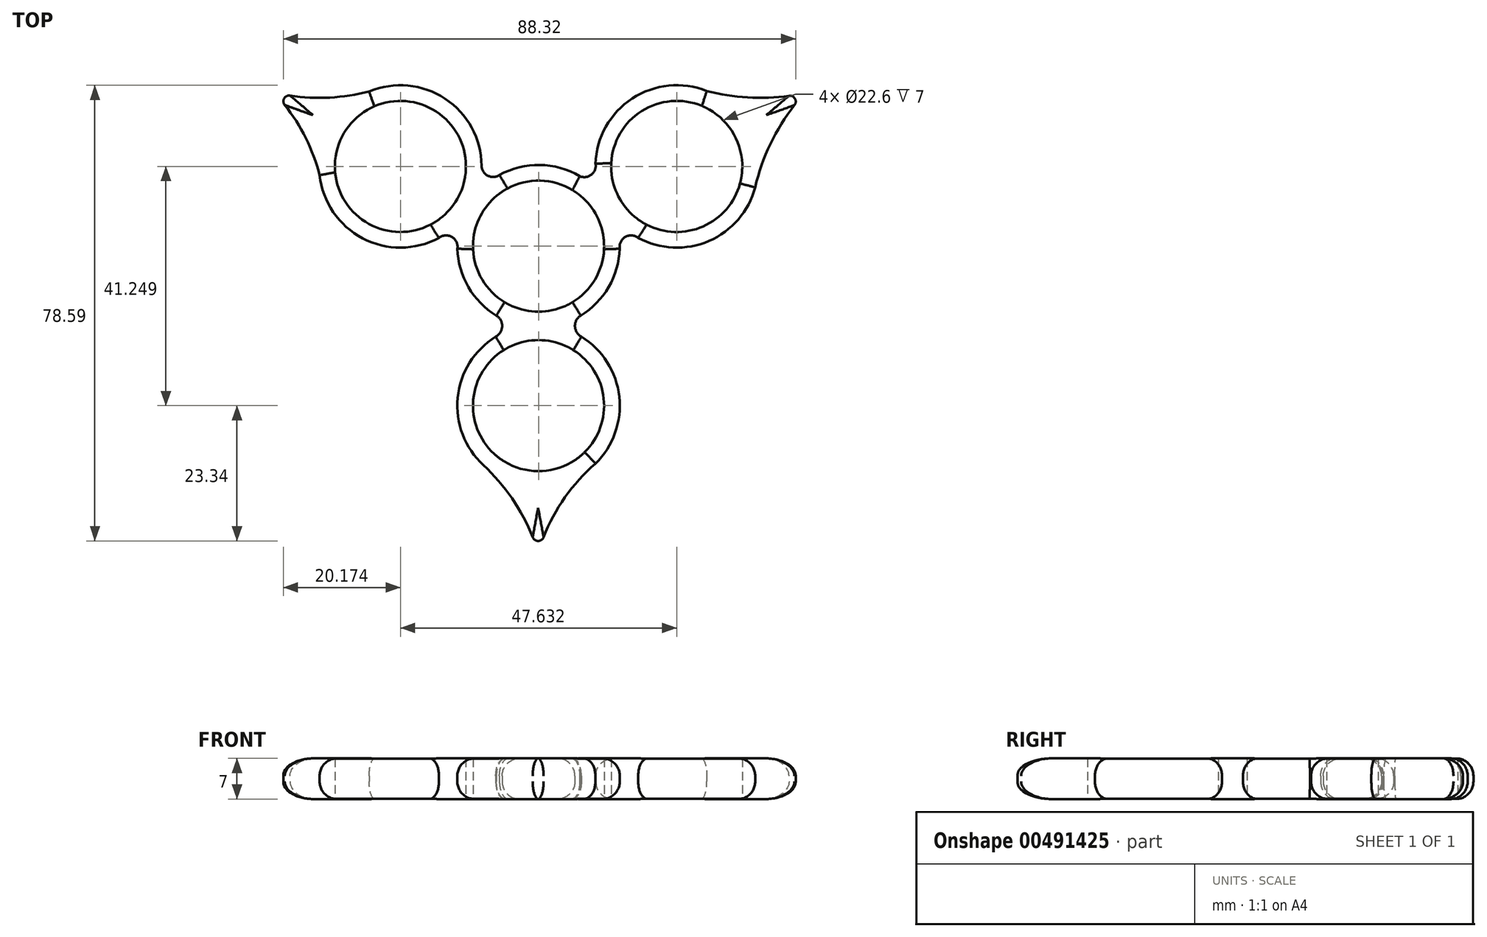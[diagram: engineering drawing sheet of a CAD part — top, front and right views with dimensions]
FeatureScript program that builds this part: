
annotation { "Feature Type Name" : "Feature", "Feature Type Description" : "" }
export const myFeature = defineFeature(function(context is Context, id is Id, definition is map)
    precondition{}
    {
        {
            var Q0;
            Q0=qCreatedBy(makeId("Top.planeOp"),FACE);
            var sketch = newSketch(context, id + "F0", { "sketchPlane" : qUnion([Q0])});
            skCircle(sketch, "E0", {"center": v(0, 0) * mm, "radius": 11.3 * mm});
            skCircle(sketch, "E1", {"center": v(0, 0) * mm, "radius": 14 * mm});
            skCircle(sketch, "E2", {"center": v(0, 0) * mm, "radius": 27.5 * mm});
            skCircle(sketch, "E3", {"center": v(-23.82, 13.75) * mm, "radius": 11.3 * mm});
            skCircle(sketch, "E4", {"center": v(23.82, 13.75) * mm, "radius": 11.3 * mm});
            skCircle(sketch, "E5", {"center": v(0, -27.5) * mm, "radius": 11.3 * mm});
            skCircle(sketch, "E6", {"center": v(-23.82, 13.75) * mm, "radius": 14 * mm});
            skCircle(sketch, "E7", {"center": v(23.82, 13.75) * mm, "radius": 14 * mm});
            skCircle(sketch, "E8", {"center": v(0, -27.5) * mm, "radius": 14 * mm});
            skArc(sketch, "E9", {"start": v(7.27, -11.97) * mm, "mid": v(6.28, -13.82) * mm, "end": v(7.38, -15.6) * mm});
            skArc(sketch, "E10", {"start": v(-7.38, -15.6) * mm, "mid": v(-6.28, -13.82) * mm, "end": v(-7.27, -11.97) * mm});
            skArc(sketch, "E11", {"start": v(6.74, 12.27) * mm, "mid": v(8.93, 12.2) * mm, "end": v(9.82, 14.2) * mm});
            skArc(sketch, "E12", {"start": v(-9.82, 13.87) * mm, "mid": v(-8.76, 12.15) * mm, "end": v(-6.74, 12.27) * mm});
            skArc(sketch, "E13", {"start": v(-14, -0.42) * mm, "mid": v(-14.95, 1.6) * mm, "end": v(-17.18, 1.42) * mm});
            skPoint(sketch, "E13.endSnap0", {"position": v(14.99, 1.42) * mm});
            skArc(sketch, "E14", {"start": v(17.18, 1.42) * mm, "mid": v(14.95, 1.6) * mm, "end": v(14, -0.42) * mm});
            skArc(sketch, "E15", {"start": v(-0.06, -52.92) * mm, "mid": v(-3.88, -44.54) * mm, "end": v(-9.82, -37.5) * mm});
            skArc(sketch, "E16", {"start": v(9.8, -37.5) * mm, "mid": v(3.76, -44.5) * mm, "end": v(-0.06, -52.92) * mm});
            skLineSegment(sketch, "E17", {"start": v(0, 0) * mm, "end": v(45.87, 26.4) * mm});
            skLineSegment(sketch, "E18", {"start": v(0, 0) * mm, "end": v(-0.06, -52.92) * mm});
            skLineSegment(sketch, "E19", {"start": v(0, 0) * mm, "end": v(-45.77, 26.56) * mm});
            skArc(sketch, "E20", {"start": v(-45.66, 26.52) * mm, "mid": v(-36.5, 25.6) * mm, "end": v(-27.41, 27.19) * mm});
            skArc(sketch, "E21", {"start": v(-37.28, 10.23) * mm, "mid": v(-40.3, 18.98) * mm, "end": v(-45.66, 26.52) * mm});
            skLineSegment(sketch, "E22", {"start": v(27.55, 27.16) * mm, "end": v(37.35, 10.15) * mm});
            skArc(sketch, "E23", {"start": v(45.87, 26.4) * mm, "mid": v(40.57, 18.82) * mm, "end": v(37.35, 10.15) * mm});
            skArc(sketch, "E24", {"start": v(27.55, 27.16) * mm, "mid": v(36.66, 25.62) * mm, "end": v(45.87, 26.4) * mm});
            skSolve(sketch);
        }
        {
            var Q0;
            {var subQ0=sQuery(id+"F0.wireOp",EDGE,"E7");var subQ1=sQuery(id+"F0.wireOp",EDGE,"E2");var subQ2=makeQuery(id+"F0.imprint","INTERSECT",VERTEX,{"disambiguationData":[OD(0.0)],"derivedFrom":[subQ1,subQ0]});Q0=makeQuery(id+"F0.imprint","IMPRINT",FACE,{"disambiguationData":[TD([[makeQuery(id+"F0.imprint","IMPRINT",EDGE,{"disambiguationData":[TD([[subQ2,-1.0]])],"derivedFrom":subQ1}),-1.0]])]});}
            var Q1;
            {var subQ0=sQuery(id+"F0.wireOp",EDGE,"E6");var subQ1=sQuery(id+"F0.wireOp",EDGE,"E2");var subQ2=makeQuery(id+"F0.imprint","INTERSECT",VERTEX,{"disambiguationData":[OD(0.0)],"derivedFrom":[subQ1,subQ0]});Q1=makeQuery(id+"F0.imprint","IMPRINT",FACE,{"disambiguationData":[TD([[makeQuery(id+"F0.imprint","IMPRINT",EDGE,{"disambiguationData":[TD([[subQ2,-1.0]])],"derivedFrom":subQ1}),-1.0]])]});}
            var Q2;
            {var subQ0=sQuery(id+"F0.wireOp",EDGE,"E8");var subQ1=sQuery(id+"F0.wireOp",EDGE,"E2");var subQ2=makeQuery(id+"F0.imprint","INTERSECT",VERTEX,{"disambiguationData":[OD(0.0)],"derivedFrom":[subQ1,subQ0]});Q2=makeQuery(id+"F0.imprint","IMPRINT",FACE,{"disambiguationData":[TD([[makeQuery(id+"F0.imprint","IMPRINT",EDGE,{"disambiguationData":[TD([[subQ2,-1.0]])],"derivedFrom":subQ1}),-1.0]])]});}
            var Q3;
            {var subQ0=sQuery(id+"F0.wireOp",EDGE,"E7");var subQ1=sQuery(id+"F0.wireOp",EDGE,"E1");var subQ2=makeQuery(id+"F0.imprint","INTERSECT",VERTEX,{"disambiguationData":[OD(0.0)],"derivedFrom":[subQ1,subQ0]});Q3=makeQuery(id+"F0.imprint","IMPRINT",FACE,{"disambiguationData":[TD([[makeQuery(id+"F0.imprint","IMPRINT",EDGE,{"disambiguationData":[TD([[subQ2,1.0]])],"derivedFrom":subQ1}),-1.0]])]});}
            var Q4;
            {var subQ4=sQuery(id+"F0.wireOp",EDGE,"E8");var subQ10=sQuery(id+"F0.wireOp",EDGE,"E1");var subQ11=makeQuery(id+"F0.imprint","INTERSECT",VERTEX,{"disambiguationData":[OD(0.0)],"derivedFrom":[subQ10,subQ4]});Q4=makeQuery(id+"F0.imprint","IMPRINT",FACE,{"disambiguationData":[TD([[makeQuery(id+"F0.imprint","IMPRINT",EDGE,{"disambiguationData":[TD([[subQ11,-1.0]])],"derivedFrom":subQ10}),-1.0]])]});}
            var Q5;
            {var subQ0=sQuery(id+"F0.wireOp",EDGE,"E11");var subQ1=sQuery(id+"F0.wireOp",EDGE,"E1");var subQ2=makeQuery(id+"F0.imprint","INTERSECT",VERTEX,{"derivedFrom":[subQ1,subQ0]});Q5=makeQuery(id+"F0.imprint","IMPRINT",FACE,{"disambiguationData":[TD([[makeQuery(id+"F0.imprint","IMPRINT",EDGE,{"disambiguationData":[TD([[subQ2,1.0]])],"derivedFrom":subQ1}),-1.0]])]});}
            var Q6;
            {var subQ0=sQuery(id+"F0.wireOp",EDGE,"E6");var subQ1=sQuery(id+"F0.wireOp",EDGE,"E1");var subQ2=makeQuery(id+"F0.imprint","INTERSECT",VERTEX,{"disambiguationData":[OD(0.0)],"derivedFrom":[subQ1,subQ0]});Q6=makeQuery(id+"F0.imprint","IMPRINT",FACE,{"disambiguationData":[TD([[makeQuery(id+"F0.imprint","IMPRINT",EDGE,{"disambiguationData":[TD([[subQ2,-1.0]])],"derivedFrom":subQ1}),1.0]])]});}
            var Q7;
            {var subQ0=sQuery(id+"F0.wireOp",EDGE,"E9");var subQ1=sQuery(id+"F0.wireOp",EDGE,"E1");var subQ2=makeQuery(id+"F0.imprint","INTERSECT",VERTEX,{"derivedFrom":[subQ1,subQ0]});Q7=makeQuery(id+"F0.imprint","IMPRINT",FACE,{"disambiguationData":[TD([[makeQuery(id+"F0.imprint","IMPRINT",EDGE,{"disambiguationData":[TD([[subQ2,1.0]])],"derivedFrom":subQ1}),-1.0]])]});}
            var Q8;
            {var subQ0=sQuery(id+"F0.wireOp",EDGE,"E10");var subQ1=sQuery(id+"F0.wireOp",EDGE,"E1");var subQ2=makeQuery(id+"F0.imprint","INTERSECT",VERTEX,{"derivedFrom":[subQ1,subQ0]});Q8=makeQuery(id+"F0.imprint","IMPRINT",FACE,{"disambiguationData":[TD([[makeQuery(id+"F0.imprint","IMPRINT",EDGE,{"disambiguationData":[TD([[subQ2,-1.0]])],"derivedFrom":subQ1}),-1.0]])]});}
            var Q9;
            {var subQ0=sQuery(id+"F0.wireOp",EDGE,"E7");var subQ10=sQuery(id+"F0.wireOp",EDGE,"E1");var subQ11=makeQuery(id+"F0.imprint","INTERSECT",VERTEX,{"disambiguationData":[OD(0.0)],"derivedFrom":[subQ10,subQ0]});Q9=makeQuery(id+"F0.imprint","IMPRINT",FACE,{"disambiguationData":[TD([[makeQuery(id+"F0.imprint","IMPRINT",EDGE,{"disambiguationData":[TD([[subQ11,-1.0]])],"derivedFrom":subQ10}),-1.0]])]});}
            var Q10;
            Q10=makeQuery(id+"F0.imprint","IMPRINT",FACE,{"disambiguationData":[TD([[makeQuery(id+"F0.imprint","IMPRINT",EDGE,{"derivedFrom":sQuery(id+"F0.wireOp",EDGE,"E0")}),-1.0]])]});
            var Q11;
            Q11=makeQuery(id+"F0.imprint","IMPRINT",FACE,{"disambiguationData":[TD([[makeQuery(id+"F0.imprint","IMPRINT",EDGE,{"derivedFrom":sQuery(id+"F0.wireOp",EDGE,"E0")}),-1.0]])]});
            var Q12;
            {var subQ0=sQuery(id+"F0.wireOp",EDGE,"E8");var subQ1=sQuery(id+"F0.wireOp",EDGE,"E1");var subQ2=makeQuery(id+"F0.imprint","INTERSECT",VERTEX,{"disambiguationData":[OD(0.0)],"derivedFrom":[subQ1,subQ0]});Q12=makeQuery(id+"F0.imprint","IMPRINT",FACE,{"disambiguationData":[TD([[makeQuery(id+"F0.imprint","IMPRINT",EDGE,{"disambiguationData":[TD([[subQ2,-1.0]])],"derivedFrom":subQ1}),1.0]])]});}
            var Q13;
            {var subQ4=sQuery(id+"F0.wireOp",EDGE,"E6");var subQ9=sQuery(id+"F0.wireOp",EDGE,"E1");var subQ10=makeQuery(id+"F0.imprint","INTERSECT",VERTEX,{"disambiguationData":[OD(0.0)],"derivedFrom":[subQ9,subQ4]});Q13=makeQuery(id+"F0.imprint","IMPRINT",FACE,{"disambiguationData":[TD([[makeQuery(id+"F0.imprint","IMPRINT",EDGE,{"disambiguationData":[TD([[subQ10,-1.0]])],"derivedFrom":subQ9}),-1.0]])]});}
            var Q14;
            {var subQ0=sQuery(id+"F0.wireOp",EDGE,"E12");var subQ1=sQuery(id+"F0.wireOp",EDGE,"E1");var subQ2=makeQuery(id+"F0.imprint","INTERSECT",VERTEX,{"disambiguationData":[OD(1.0)],"derivedFrom":[subQ1,subQ0]});Q14=makeQuery(id+"F0.imprint","IMPRINT",FACE,{"disambiguationData":[TD([[makeQuery(id+"F0.imprint","IMPRINT",EDGE,{"disambiguationData":[TD([[subQ2,-1.0]])],"derivedFrom":subQ1}),-1.0]])]});}
            var Q15;
            {var subQ0=sQuery(id+"F0.wireOp",EDGE,"E6");var subQ1=sQuery(id+"F0.wireOp",EDGE,"E1");var subQ2=makeQuery(id+"F0.imprint","INTERSECT",VERTEX,{"disambiguationData":[OD(1.0)],"derivedFrom":[subQ1,subQ0]});Q15=makeQuery(id+"F0.imprint","IMPRINT",FACE,{"disambiguationData":[TD([[makeQuery(id+"F0.imprint","IMPRINT",EDGE,{"disambiguationData":[TD([[subQ2,-1.0]])],"derivedFrom":subQ1}),-1.0]])]});}
            var Q16;
            {var subQ0=sQuery(id+"F0.wireOp",EDGE,"E7");var subQ1=sQuery(id+"F0.wireOp",EDGE,"E1");var subQ2=makeQuery(id+"F0.imprint","INTERSECT",VERTEX,{"disambiguationData":[OD(0.0)],"derivedFrom":[subQ1,subQ0]});Q16=makeQuery(id+"F0.imprint","IMPRINT",FACE,{"disambiguationData":[TD([[makeQuery(id+"F0.imprint","IMPRINT",EDGE,{"disambiguationData":[TD([[subQ2,-1.0]])],"derivedFrom":subQ1}),1.0]])]});}
            var Q17;
            {var subQ0=sQuery(id+"F0.wireOp",EDGE,"E7");var subQ1=sQuery(id+"F0.wireOp",EDGE,"E2");var subQ2=makeQuery(id+"F0.imprint","INTERSECT",VERTEX,{"disambiguationData":[OD(1.0)],"derivedFrom":[subQ1,subQ0]});Q17=makeQuery(id+"F0.imprint","IMPRINT",FACE,{"disambiguationData":[TD([[makeQuery(id+"F0.imprint","IMPRINT",EDGE,{"disambiguationData":[TD([[subQ2,1.0]])],"derivedFrom":subQ1}),-1.0]])]});}
            var Q18;
            {var subQ1=sQuery(id+"F0.wireOp",EDGE,"3PTmMetB-9Mq9-OfqD-WaSR-vOR6SDGipExO.left");var subQ4=sQuery(id+"F0.wireOp",EDGE,"E4");var subQ5=makeQuery(id+"F0.imprint","INTERSECT",VERTEX,{"derivedFrom":[subQ4,subQ1]});Q18=makeQuery(id+"F0.imprint","IMPRINT",FACE,{"disambiguationData":[TD([[makeQuery(id+"F0.imprint","IMPRINT",EDGE,{"disambiguationData":[TD([[subQ5,1.0]])],"derivedFrom":subQ4}),-1.0]])]});}
            var Q19;
            {var subQ1=sQuery(id+"F0.wireOp",EDGE,"9Et0mAI1-HBt8-Chc9-DNCY-ShBSqTFfpHgo.left");var subQ4=sQuery(id+"F0.wireOp",EDGE,"E3");var subQ5=makeQuery(id+"F0.imprint","INTERSECT",VERTEX,{"derivedFrom":[subQ4,subQ1]});Q19=makeQuery(id+"F0.imprint","IMPRINT",FACE,{"disambiguationData":[TD([[makeQuery(id+"F0.imprint","IMPRINT",EDGE,{"disambiguationData":[TD([[subQ5,-1.0]])],"derivedFrom":subQ4}),-1.0]])]});}
            var Q20;
            {var subQ0=sQuery(id+"F0.wireOp",EDGE,"E6");var subQ1=sQuery(id+"F0.wireOp",EDGE,"E2");var subQ2=makeQuery(id+"F0.imprint","INTERSECT",VERTEX,{"disambiguationData":[OD(1.0)],"derivedFrom":[subQ1,subQ0]});Q20=makeQuery(id+"F0.imprint","IMPRINT",FACE,{"disambiguationData":[TD([[makeQuery(id+"F0.imprint","IMPRINT",EDGE,{"disambiguationData":[TD([[subQ2,1.0]])],"derivedFrom":subQ1}),-1.0]])]});}
            var Q21;
            {var subQ0=sQuery(id+"F0.wireOp",EDGE,"0O0kyQyX-SNUq-BMQf-ScT6-pGwFIUG6Fi4E");var subQ1=sQuery(id+"F0.wireOp",EDGE,"E6");var subQ2=makeQuery(id+"F0.imprint","INTERSECT",VERTEX,{"derivedFrom":[subQ1,subQ0]});Q21=makeQuery(id+"F0.imprint","IMPRINT",FACE,{"disambiguationData":[TD([[makeQuery(id+"F0.imprint","IMPRINT",EDGE,{"disambiguationData":[TD([[subQ2,-1.0]])],"derivedFrom":subQ1}),-1.0]])]});}
            var Q22;
            {var subQ0=sQuery(id+"F0.wireOp",EDGE,"E15");var subQ1=sQuery(id+"F0.wireOp",EDGE,"E8");var subQ2=makeQuery(id+"F0.imprint","INTERSECT",VERTEX,{"derivedFrom":[subQ1,subQ0]});Q22=makeQuery(id+"F0.imprint","IMPRINT",FACE,{"disambiguationData":[TD([[makeQuery(id+"F0.imprint","IMPRINT",EDGE,{"disambiguationData":[TD([[subQ2,-1.0]])],"derivedFrom":subQ1}),-1.0]])]});}
            var Q23;
            {var subQ0=sQuery(id+"F0.wireOp",EDGE,"E19");var subQ1=sQuery(id+"F0.wireOp",EDGE,"E1");var subQ2=makeQuery(id+"F0.imprint","INTERSECT",VERTEX,{"derivedFrom":[subQ1,subQ0]});Q23=makeQuery(id+"F0.imprint","IMPRINT",FACE,{"disambiguationData":[TD([[makeQuery(id+"F0.imprint","IMPRINT",EDGE,{"disambiguationData":[TD([[subQ2,-1.0]])],"derivedFrom":subQ1}),1.0]])]});}
            var Q24;
            {var subQ5=sQuery(id+"F0.wireOp",EDGE,"E19");var subQ6=sQuery(id+"F0.wireOp",EDGE,"E1");var subQ7=makeQuery(id+"F0.imprint","INTERSECT",VERTEX,{"derivedFrom":[subQ6,subQ5]});Q24=makeQuery(id+"F0.imprint","IMPRINT",FACE,{"disambiguationData":[TD([[makeQuery(id+"F0.imprint","IMPRINT",EDGE,{"disambiguationData":[TD([[subQ7,-1.0]])],"derivedFrom":subQ6}),-1.0]])]});}
            var Q25;
            {var subQ7=sQuery(id+"F0.wireOp",EDGE,"E18");var subQ9=sQuery(id+"F0.wireOp",EDGE,"E1");var subQ10=makeQuery(id+"F0.imprint","INTERSECT",VERTEX,{"derivedFrom":[subQ9,subQ7]});Q25=makeQuery(id+"F0.imprint","IMPRINT",FACE,{"disambiguationData":[TD([[makeQuery(id+"F0.imprint","IMPRINT",EDGE,{"disambiguationData":[TD([[subQ10,-1.0]])],"derivedFrom":subQ9}),-1.0]])]});}
            var Q26;
            {var subQ0=sQuery(id+"F0.wireOp",EDGE,"E18");var subQ1=sQuery(id+"F0.wireOp",EDGE,"E1");var subQ2=makeQuery(id+"F0.imprint","INTERSECT",VERTEX,{"derivedFrom":[subQ1,subQ0]});Q26=makeQuery(id+"F0.imprint","IMPRINT",FACE,{"disambiguationData":[TD([[makeQuery(id+"F0.imprint","IMPRINT",EDGE,{"disambiguationData":[TD([[subQ2,-1.0]])],"derivedFrom":subQ1}),1.0]])]});}
            var Q27;
            {var subQ1=sQuery(id+"F0.wireOp",EDGE,"E8");var subQ6=sQuery(id+"F0.wireOp",EDGE,"E2");var subQ10=makeQuery(id+"F0.imprint","INTERSECT",VERTEX,{"disambiguationData":[OD(1.0)],"derivedFrom":[subQ6,subQ1]});Q27=makeQuery(id+"F0.imprint","IMPRINT",FACE,{"disambiguationData":[TD([[makeQuery(id+"F0.imprint","IMPRINT",EDGE,{"disambiguationData":[TD([[subQ10,1.0]])],"derivedFrom":subQ6}),-1.0]])]});}
            var Q28;
            {var subQ0=sQuery(id+"F0.wireOp",EDGE,"E16");var subQ1=sQuery(id+"F0.wireOp",EDGE,"E8");var subQ2=makeQuery(id+"F0.imprint","INTERSECT",VERTEX,{"disambiguationData":[OD(1.0)],"derivedFrom":[subQ1,subQ0]});Q28=makeQuery(id+"F0.imprint","IMPRINT",FACE,{"disambiguationData":[TD([[makeQuery(id+"F0.imprint","IMPRINT",EDGE,{"disambiguationData":[TD([[subQ2,1.0]])],"derivedFrom":subQ1}),-1.0]])]});}
            var Q29;
            {var subQ7=sQuery(id+"F0.wireOp",EDGE,"E17");var subQ9=sQuery(id+"F0.wireOp",EDGE,"E1");var subQ12=makeQuery(id+"F0.imprint","INTERSECT",VERTEX,{"derivedFrom":[subQ9,subQ7]});Q29=makeQuery(id+"F0.imprint","IMPRINT",FACE,{"disambiguationData":[TD([[makeQuery(id+"F0.imprint","IMPRINT",EDGE,{"disambiguationData":[TD([[subQ12,-1.0]])],"derivedFrom":subQ9}),-1.0]])]});}
            var Q30;
            {var subQ0=sQuery(id+"F0.wireOp",EDGE,"2c0cabc1-3ef5-4402-aa69-39098cf523b3");var subQ1=sQuery(id+"F0.wireOp",EDGE,"E7");var subQ2=makeQuery(id+"F0.imprint","INTERSECT",VERTEX,{"derivedFrom":[subQ1,subQ0]});Q30=makeQuery(id+"F0.imprint","IMPRINT",FACE,{"disambiguationData":[TD([[makeQuery(id+"F0.imprint","IMPRINT",EDGE,{"disambiguationData":[TD([[subQ2,1.0]])],"derivedFrom":subQ1}),-1.0]])]});}
            var Q31;
            {var subQ0=sQuery(id+"F0.wireOp",EDGE,"E17");var subQ1=sQuery(id+"F0.wireOp",EDGE,"E1");var subQ2=makeQuery(id+"F0.imprint","INTERSECT",VERTEX,{"derivedFrom":[subQ1,subQ0]});Q31=makeQuery(id+"F0.imprint","IMPRINT",FACE,{"disambiguationData":[TD([[makeQuery(id+"F0.imprint","IMPRINT",EDGE,{"disambiguationData":[TD([[subQ2,-1.0]])],"derivedFrom":subQ1}),1.0]])]});}
            var Q32;
            {var subQ0=sQuery(id+"F0.wireOp",EDGE,"E20");var subQ1=sQuery(id+"F0.wireOp",EDGE,"E6");var subQ2=makeQuery(id+"F0.imprint","INTERSECT",VERTEX,{"derivedFrom":[subQ1,subQ0]});Q32=makeQuery(id+"F0.imprint","IMPRINT",FACE,{"disambiguationData":[TD([[makeQuery(id+"F0.imprint","IMPRINT",EDGE,{"disambiguationData":[TD([[subQ2,-1.0]])],"derivedFrom":subQ1}),-1.0]])]});}
            var Q33;
            {var subQ5=sQuery(id+"F0.wireOp",EDGE,"E17");var subQ6=sQuery(id+"F0.wireOp",EDGE,"E4");var subQ7=makeQuery(id+"F0.imprint","INTERSECT",VERTEX,{"disambiguationData":[OD(0.0)],"derivedFrom":[subQ6,subQ5]});Q33=makeQuery(id+"F0.imprint","IMPRINT",FACE,{"disambiguationData":[TD([[makeQuery(id+"F0.imprint","IMPRINT",EDGE,{"disambiguationData":[TD([[subQ7,-1.0]])],"derivedFrom":subQ6}),-1.0]])]});}
            var Q34;
            {var subQ4=sQuery(id+"F0.wireOp",EDGE,"E4");var subQ6=sQuery(id+"F0.wireOp",EDGE,"E17");var subQ8=makeQuery(id+"F0.imprint","INTERSECT",VERTEX,{"disambiguationData":[OD(0.0)],"derivedFrom":[subQ4,subQ6]});Q34=makeQuery(id+"F0.imprint","IMPRINT",FACE,{"disambiguationData":[TD([[makeQuery(id+"F0.imprint","IMPRINT",EDGE,{"disambiguationData":[TD([[subQ8,1.0]])],"derivedFrom":subQ4}),-1.0]])]});}
            var Q35;
            {var subQ0=sQuery(id+"F0.wireOp",EDGE,"E17");var subQ1=sQuery(id+"F0.wireOp",EDGE,"E7");var subQ2=makeQuery(id+"F0.imprint","INTERSECT",VERTEX,{"disambiguationData":[OD(0.0)],"derivedFrom":[subQ1,subQ0]});Q35=makeQuery(id+"F0.imprint","IMPRINT",FACE,{"disambiguationData":[TD([[makeQuery(id+"F0.imprint","IMPRINT",EDGE,{"disambiguationData":[TD([[subQ2,1.0]])],"derivedFrom":subQ1}),-1.0]])]});}
            extrude(context, id + "F1", {"entities" : qUnion([Q0, Q1, Q2, Q3, Q4, Q5, Q6, Q7, Q8, Q9, Q10, Q11, Q12, Q13, Q14, Q15, Q16, Q17, Q18, Q19, Q20, Q21, Q22, Q23, Q24, Q25, Q26, Q27, Q28, Q29, Q30, Q31, Q32, Q33, Q34, Q35]), "depth" : 7 * mm});
        }
        {
            var Q0;
            Q0=makeQuery(id+"F1.opExtrude","SWEPT_EDGE",EDGE,{"disambiguationData":[OSD([sQuery(id+"F0.wireOp",EDGE,"E15"),sQuery(id+"F0.wireOp",EDGE,"E16"),sQuery(id+"F0.wireOp",EDGE,"E18")])]});
            var Q1;
            Q1=makeQuery(id+"F1.opExtrude","SWEPT_EDGE",EDGE,{"disambiguationData":[OSD([sQuery(id+"F0.wireOp",EDGE,"E20"),sQuery(id+"F0.wireOp",EDGE,"E21")])]});
            var Q2;
            Q2=makeQuery(id+"F1.opExtrude","SWEPT_EDGE",EDGE,{"disambiguationData":[OSD([sQuery(id+"F0.wireOp",EDGE,"E17"),sQuery(id+"F0.wireOp",EDGE,"E23"),sQuery(id+"F0.wireOp",EDGE,"E24")])]});
            fillet(context, id + "F2", {"entities" : qUnion([Q0, Q1, Q2]), "radius" : 1 * mm, "tangentPropagation" : true, "allowEdgeOverflow" : false});
        }
        {
            var Q0;
            Q0=makeQuery(id+"F1.opExtrude","CAP_EDGE",EDGE,{"disambiguationData":[OSD([sQuery(id+"F0.wireOp",EDGE,"E21")])],"isStart":false});
            var Q1;
            Q1=makeQuery(id+"F1.opExtrude","CAP_EDGE",EDGE,{"disambiguationData":[OSD([sQuery(id+"F0.wireOp",EDGE,"E20")])],"isStart":false});
            var Q2;
            {var subQ0=sQuery(id+"F0.wireOp",EDGE,"E6");Q2=makeQuery(id+"F1.opExtrude","CAP_EDGE",EDGE,{"disambiguationData":[OSD([subQ0]),TDD([makeQuery(id+"F0.imprint","IMPRINT",EDGE,{"disambiguationData":[TD([[makeQuery(id+"F0.imprint","INTERSECT",VERTEX,{"derivedFrom":[subQ0,sQuery(id+"F0.wireOp",EDGE,"E12")]}),-1.0]])],"derivedFrom":subQ0}),makeQuery(id+"F0.imprint","IMPRINT",EDGE,{"disambiguationData":[TD([[makeQuery(id+"F0.imprint","INTERSECT",VERTEX,{"derivedFrom":[subQ0,sQuery(id+"F0.wireOp",EDGE,"E20")]}),1.0]])],"derivedFrom":subQ0})])],"isStart":false});}
            var Q3;
            {var subQ0=sQuery(id+"F0.wireOp",EDGE,"E6");Q3=makeQuery(id+"F1.opExtrude","CAP_EDGE",EDGE,{"disambiguationData":[OSD([subQ0]),TDD([makeQuery(id+"F0.imprint","IMPRINT",EDGE,{"disambiguationData":[TD([[makeQuery(id+"F0.imprint","INTERSECT",VERTEX,{"derivedFrom":[subQ0,sQuery(id+"F0.wireOp",EDGE,"E21")]}),-1.0]])],"derivedFrom":subQ0}),makeQuery(id+"F0.imprint","IMPRINT",EDGE,{"disambiguationData":[TD([[makeQuery(id+"F0.imprint","INTERSECT",VERTEX,{"disambiguationData":[OD(0.0)],"derivedFrom":[subQ0,sQuery(id+"F0.wireOp",EDGE,"E13")]}),1.0]])],"derivedFrom":subQ0})])],"isStart":false});}
            var Q4;
            Q4=makeQuery(id+"F1.opExtrude","CAP_EDGE",EDGE,{"disambiguationData":[OSD([sQuery(id+"F0.wireOp",EDGE,"E13")])],"isStart":false});
            var Q5;
            {var subQ0=sQuery(id+"F0.wireOp",EDGE,"E1");Q5=makeQuery(id+"F1.opExtrude","CAP_EDGE",EDGE,{"disambiguationData":[OSD([subQ0]),TDD([makeQuery(id+"F0.imprint","IMPRINT",EDGE,{"disambiguationData":[TD([[makeQuery(id+"F0.imprint","INTERSECT",VERTEX,{"derivedFrom":[subQ0,sQuery(id+"F0.wireOp",EDGE,"E10")]}),1.0]])],"derivedFrom":subQ0})])],"isStart":false});}
            var Q6;
            Q6=makeQuery(id+"F1.opExtrude","CAP_EDGE",EDGE,{"disambiguationData":[OSD([sQuery(id+"F0.wireOp",EDGE,"E10")])],"isStart":false});
            var Q7;
            {var subQ0=sQuery(id+"F0.wireOp",EDGE,"E8");Q7=makeQuery(id+"F1.opExtrude","CAP_EDGE",EDGE,{"disambiguationData":[OSD([subQ0]),TDD([makeQuery(id+"F0.imprint","IMPRINT",EDGE,{"disambiguationData":[TD([[makeQuery(id+"F0.imprint","INTERSECT",VERTEX,{"disambiguationData":[OD(0.0)],"derivedFrom":[subQ0,sQuery(id+"F0.wireOp",EDGE,"E10")]}),-1.0]])],"derivedFrom":subQ0}),makeQuery(id+"F0.imprint","IMPRINT",EDGE,{"disambiguationData":[TD([[makeQuery(id+"F0.imprint","INTERSECT",VERTEX,{"derivedFrom":[subQ0,sQuery(id+"F0.wireOp",EDGE,"E15")]}),1.0]])],"derivedFrom":subQ0})])],"isStart":false});}
            var Q8;
            Q8=makeQuery(id+"F1.opExtrude","CAP_EDGE",EDGE,{"disambiguationData":[OSD([sQuery(id+"F0.wireOp",EDGE,"E15")])],"isStart":false});
            var Q9;
            Q9=makeQuery(id+"F1.opExtrude","CAP_EDGE",EDGE,{"disambiguationData":[OSD([sQuery(id+"F0.wireOp",EDGE,"E16")])],"isStart":false});
            var Q10;
            {var subQ0=sQuery(id+"F0.wireOp",EDGE,"E16");var subQ1=sQuery(id+"F0.wireOp",EDGE,"E15");Q10=makeQuery(id+"F2.opFillet","BLEND_EDGE",EDGE,{"blendedFrom":[makeQuery(id+"F1.opExtrude","SWEPT_EDGE",EDGE,{"disambiguationData":[OSD([subQ1,subQ0,sQuery(id+"F0.wireOp",EDGE,"E18")])]}),makeQuery(id+"F1.opExtrude","CAP_FACE",FACE,{"disambiguationData":[OSD([sQuery(id+"F0.wireOp",EDGE,"E0"),sQuery(id+"F0.wireOp",EDGE,"E1"),sQuery(id+"F0.wireOp",EDGE,"E3"),sQuery(id+"F0.wireOp",EDGE,"E4"),sQuery(id+"F0.wireOp",EDGE,"E5"),sQuery(id+"F0.wireOp",EDGE,"E6"),sQuery(id+"F0.wireOp",EDGE,"E7"),sQuery(id+"F0.wireOp",EDGE,"E8"),sQuery(id+"F0.wireOp",EDGE,"E9"),sQuery(id+"F0.wireOp",EDGE,"E10"),sQuery(id+"F0.wireOp",EDGE,"E11"),sQuery(id+"F0.wireOp",EDGE,"E12"),sQuery(id+"F0.wireOp",EDGE,"E13"),sQuery(id+"F0.wireOp",EDGE,"E14"),subQ1,subQ0,sQuery(id+"F0.wireOp",EDGE,"E20"),sQuery(id+"F0.wireOp",EDGE,"E21"),sQuery(id+"F0.wireOp",EDGE,"E23"),sQuery(id+"F0.wireOp",EDGE,"E24")])],"isStart":false})],"blendedInto":[makeQuery(id+"F1.opExtrude","CAP_FACE",FACE,{"disambiguationData":[OSD([sQuery(id+"F0.wireOp",EDGE,"E0"),sQuery(id+"F0.wireOp",EDGE,"E1"),sQuery(id+"F0.wireOp",EDGE,"E3"),sQuery(id+"F0.wireOp",EDGE,"E4"),sQuery(id+"F0.wireOp",EDGE,"E5"),sQuery(id+"F0.wireOp",EDGE,"E6"),sQuery(id+"F0.wireOp",EDGE,"E7"),sQuery(id+"F0.wireOp",EDGE,"E8"),sQuery(id+"F0.wireOp",EDGE,"E9"),sQuery(id+"F0.wireOp",EDGE,"E10"),sQuery(id+"F0.wireOp",EDGE,"E11"),sQuery(id+"F0.wireOp",EDGE,"E12"),sQuery(id+"F0.wireOp",EDGE,"E13"),sQuery(id+"F0.wireOp",EDGE,"E14"),subQ1,subQ0,sQuery(id+"F0.wireOp",EDGE,"E20"),sQuery(id+"F0.wireOp",EDGE,"E21"),sQuery(id+"F0.wireOp",EDGE,"E23"),sQuery(id+"F0.wireOp",EDGE,"E24")])],"isStart":false})]});}
            var Q11;
            {var subQ0=sQuery(id+"F0.wireOp",EDGE,"E8");Q11=makeQuery(id+"F1.opExtrude","CAP_EDGE",EDGE,{"disambiguationData":[OSD([subQ0]),TDD([makeQuery(id+"F0.imprint","IMPRINT",EDGE,{"disambiguationData":[TD([[makeQuery(id+"F0.imprint","INTERSECT",VERTEX,{"disambiguationData":[OD(0.0)],"derivedFrom":[subQ0,sQuery(id+"F0.wireOp",EDGE,"E9")]}),1.0]])],"derivedFrom":subQ0}),makeQuery(id+"F0.imprint","IMPRINT",EDGE,{"disambiguationData":[TD([[makeQuery(id+"F0.imprint","INTERSECT",VERTEX,{"disambiguationData":[OD(0.0)],"derivedFrom":[subQ0,sQuery(id+"F0.wireOp",EDGE,"E16")]}),-1.0]])],"derivedFrom":subQ0})])],"isStart":false});}
            var Q12;
            Q12=makeQuery(id+"F1.opExtrude","CAP_EDGE",EDGE,{"disambiguationData":[OSD([sQuery(id+"F0.wireOp",EDGE,"E9")])],"isStart":false});
            var Q13;
            {var subQ0=sQuery(id+"F0.wireOp",EDGE,"E1");Q13=makeQuery(id+"F1.opExtrude","CAP_EDGE",EDGE,{"disambiguationData":[OSD([subQ0]),TDD([makeQuery(id+"F0.imprint","IMPRINT",EDGE,{"disambiguationData":[TD([[makeQuery(id+"F0.imprint","INTERSECT",VERTEX,{"derivedFrom":[subQ0,sQuery(id+"F0.wireOp",EDGE,"E9")]}),-1.0]])],"derivedFrom":subQ0})])],"isStart":false});}
            var Q14;
            Q14=makeQuery(id+"F1.opExtrude","CAP_EDGE",EDGE,{"disambiguationData":[OSD([sQuery(id+"F0.wireOp",EDGE,"E14")])],"isStart":false});
            var Q15;
            {var subQ0=sQuery(id+"F0.wireOp",EDGE,"E7");var subQ1=makeQuery(id+"F0.imprint","INTERSECT",VERTEX,{"disambiguationData":[OD(0.0)],"derivedFrom":[sQuery(id+"F0.wireOp",EDGE,"E2"),subQ0]});Q15=makeQuery(id+"F1.opExtrude","CAP_EDGE",EDGE,{"disambiguationData":[OSD([subQ0]),TDD([makeQuery(id+"F0.imprint","IMPRINT",EDGE,{"disambiguationData":[TD([[makeQuery(id+"F0.imprint","INTERSECT",VERTEX,{"disambiguationData":[OD(0.0)],"derivedFrom":[subQ0,sQuery(id+"F0.wireOp",EDGE,"E14")]}),-1.0]])],"derivedFrom":subQ0}),makeQuery(id+"F0.imprint","IMPRINT",EDGE,{"disambiguationData":[TD([[subQ1,-1.0]])],"derivedFrom":subQ0})])],"isStart":false});}
            var Q16;
            Q16=makeQuery(id+"F1.opExtrude","CAP_EDGE",EDGE,{"disambiguationData":[OSD([sQuery(id+"F0.wireOp",EDGE,"E23")])],"isStart":false});
            var Q17;
            Q17=makeQuery(id+"F1.opExtrude","CAP_EDGE",EDGE,{"disambiguationData":[OSD([sQuery(id+"F0.wireOp",EDGE,"E24")])],"isStart":false});
            var Q18;
            {var subQ0=sQuery(id+"F0.wireOp",EDGE,"E7");var subQ1=makeQuery(id+"F0.imprint","INTERSECT",VERTEX,{"disambiguationData":[OD(1.0)],"derivedFrom":[sQuery(id+"F0.wireOp",EDGE,"E2"),subQ0]});Q18=makeQuery(id+"F1.opExtrude","CAP_EDGE",EDGE,{"disambiguationData":[OSD([subQ0]),TDD([makeQuery(id+"F0.imprint","IMPRINT",EDGE,{"disambiguationData":[TD([[subQ1,1.0]])],"derivedFrom":subQ0}),makeQuery(id+"F0.imprint","IMPRINT",EDGE,{"disambiguationData":[TD([[makeQuery(id+"F0.imprint","INTERSECT",VERTEX,{"disambiguationData":[OD(0.0)],"derivedFrom":[subQ0,sQuery(id+"F0.wireOp",EDGE,"E11")]}),1.0]])],"derivedFrom":subQ0})])],"isStart":false});}
            var Q19;
            Q19=makeQuery(id+"F1.opExtrude","CAP_EDGE",EDGE,{"disambiguationData":[OSD([sQuery(id+"F0.wireOp",EDGE,"E11")])],"isStart":false});
            var Q20;
            {var subQ0=sQuery(id+"F0.wireOp",EDGE,"E1");Q20=makeQuery(id+"F1.opExtrude","CAP_EDGE",EDGE,{"disambiguationData":[OSD([subQ0]),TDD([makeQuery(id+"F0.imprint","IMPRINT",EDGE,{"disambiguationData":[TD([[makeQuery(id+"F0.imprint","INTERSECT",VERTEX,{"disambiguationData":[OD(0.0)],"derivedFrom":[subQ0,sQuery(id+"F0.wireOp",EDGE,"E12")]}),1.0]])],"derivedFrom":subQ0})])],"isStart":false});}
            var Q21;
            Q21=makeQuery(id+"F1.opExtrude","CAP_EDGE",EDGE,{"disambiguationData":[OSD([sQuery(id+"F0.wireOp",EDGE,"E12")])],"isStart":false});
            fillet(context, id + "F3", {"entities" : qUnion([Q0, Q1, Q2, Q3, Q4, Q5, Q6, Q7, Q8, Q9, Q10, Q11, Q12, Q13, Q14, Q15, Q16, Q17, Q18, Q19, Q20, Q21]), "radius" : 3 * mm, "tangentPropagation" : true, "allowEdgeOverflow" : false});
        }
        {
            var Q0;
            {var subQ0=sQuery(id+"F0.wireOp",EDGE,"E21");var subQ1=sQuery(id+"F0.wireOp",EDGE,"E20");Q0=makeQuery(id+"F2.opFillet","BLEND_EDGE",EDGE,{"blendedFrom":[makeQuery(id+"F1.opExtrude","SWEPT_EDGE",EDGE,{"disambiguationData":[OSD([subQ1,subQ0])]}),makeQuery(id+"F1.opExtrude","CAP_FACE",FACE,{"disambiguationData":[OSD([sQuery(id+"F0.wireOp",EDGE,"E0"),sQuery(id+"F0.wireOp",EDGE,"E1"),sQuery(id+"F0.wireOp",EDGE,"E3"),sQuery(id+"F0.wireOp",EDGE,"E4"),sQuery(id+"F0.wireOp",EDGE,"E5"),sQuery(id+"F0.wireOp",EDGE,"E6"),sQuery(id+"F0.wireOp",EDGE,"E7"),sQuery(id+"F0.wireOp",EDGE,"E8"),sQuery(id+"F0.wireOp",EDGE,"E9"),sQuery(id+"F0.wireOp",EDGE,"E10"),sQuery(id+"F0.wireOp",EDGE,"E11"),sQuery(id+"F0.wireOp",EDGE,"E12"),sQuery(id+"F0.wireOp",EDGE,"E13"),sQuery(id+"F0.wireOp",EDGE,"E14"),sQuery(id+"F0.wireOp",EDGE,"E15"),sQuery(id+"F0.wireOp",EDGE,"E16"),subQ1,subQ0,sQuery(id+"F0.wireOp",EDGE,"E23"),sQuery(id+"F0.wireOp",EDGE,"E24")])],"isStart":true})],"blendedInto":[makeQuery(id+"F1.opExtrude","CAP_FACE",FACE,{"disambiguationData":[OSD([sQuery(id+"F0.wireOp",EDGE,"E0"),sQuery(id+"F0.wireOp",EDGE,"E1"),sQuery(id+"F0.wireOp",EDGE,"E3"),sQuery(id+"F0.wireOp",EDGE,"E4"),sQuery(id+"F0.wireOp",EDGE,"E5"),sQuery(id+"F0.wireOp",EDGE,"E6"),sQuery(id+"F0.wireOp",EDGE,"E7"),sQuery(id+"F0.wireOp",EDGE,"E8"),sQuery(id+"F0.wireOp",EDGE,"E9"),sQuery(id+"F0.wireOp",EDGE,"E10"),sQuery(id+"F0.wireOp",EDGE,"E11"),sQuery(id+"F0.wireOp",EDGE,"E12"),sQuery(id+"F0.wireOp",EDGE,"E13"),sQuery(id+"F0.wireOp",EDGE,"E14"),sQuery(id+"F0.wireOp",EDGE,"E15"),sQuery(id+"F0.wireOp",EDGE,"E16"),subQ1,subQ0,sQuery(id+"F0.wireOp",EDGE,"E23"),sQuery(id+"F0.wireOp",EDGE,"E24")])],"isStart":true})]});}
            var Q1;
            Q1=makeQuery(id+"F1.opExtrude","CAP_EDGE",EDGE,{"disambiguationData":[OSD([sQuery(id+"F0.wireOp",EDGE,"E21")])],"isStart":true});
            var Q2;
            Q2=makeQuery(id+"F1.opExtrude","CAP_EDGE",EDGE,{"disambiguationData":[OSD([sQuery(id+"F0.wireOp",EDGE,"E20")])],"isStart":true});
            var Q3;
            {var subQ0=sQuery(id+"F0.wireOp",EDGE,"E6");Q3=makeQuery(id+"F1.opExtrude","CAP_EDGE",EDGE,{"disambiguationData":[OSD([subQ0]),TDD([makeQuery(id+"F0.imprint","IMPRINT",EDGE,{"disambiguationData":[TD([[makeQuery(id+"F0.imprint","INTERSECT",VERTEX,{"derivedFrom":[subQ0,sQuery(id+"F0.wireOp",EDGE,"E21")]}),-1.0]])],"derivedFrom":subQ0}),makeQuery(id+"F0.imprint","IMPRINT",EDGE,{"disambiguationData":[TD([[makeQuery(id+"F0.imprint","INTERSECT",VERTEX,{"disambiguationData":[OD(0.0)],"derivedFrom":[subQ0,sQuery(id+"F0.wireOp",EDGE,"E13")]}),1.0]])],"derivedFrom":subQ0})])],"isStart":true});}
            var Q4;
            Q4=makeQuery(id+"F1.opExtrude","CAP_EDGE",EDGE,{"disambiguationData":[OSD([sQuery(id+"F0.wireOp",EDGE,"E13")])],"isStart":true});
            var Q5;
            Q5=makeQuery(id+"F1.opExtrude","CAP_EDGE",EDGE,{"disambiguationData":[OSD([sQuery(id+"F0.wireOp",EDGE,"E12")])],"isStart":true});
            var Q6;
            Q6=makeQuery(id+"F1.opExtrude","CAP_EDGE",EDGE,{"disambiguationData":[OSD([sQuery(id+"F0.wireOp",EDGE,"E11")])],"isStart":true});
            var Q7;
            Q7=makeQuery(id+"F1.opExtrude","CAP_EDGE",EDGE,{"disambiguationData":[OSD([sQuery(id+"F0.wireOp",EDGE,"E14")])],"isStart":true});
            var Q8;
            Q8=makeQuery(id+"F1.opExtrude","CAP_EDGE",EDGE,{"disambiguationData":[OSD([sQuery(id+"F0.wireOp",EDGE,"E9")])],"isStart":true});
            var Q9;
            Q9=makeQuery(id+"F1.opExtrude","CAP_EDGE",EDGE,{"disambiguationData":[OSD([sQuery(id+"F0.wireOp",EDGE,"E10")])],"isStart":true});
            var Q10;
            {var subQ0=sQuery(id+"F0.wireOp",EDGE,"E1");Q10=makeQuery(id+"F1.opExtrude","CAP_EDGE",EDGE,{"disambiguationData":[OSD([subQ0]),TDD([makeQuery(id+"F0.imprint","IMPRINT",EDGE,{"disambiguationData":[TD([[makeQuery(id+"F0.imprint","INTERSECT",VERTEX,{"derivedFrom":[subQ0,sQuery(id+"F0.wireOp",EDGE,"E10")]}),1.0]])],"derivedFrom":subQ0})])],"isStart":true});}
            var Q11;
            {var subQ0=sQuery(id+"F0.wireOp",EDGE,"E1");Q11=makeQuery(id+"F1.opExtrude","CAP_EDGE",EDGE,{"disambiguationData":[OSD([subQ0]),TDD([makeQuery(id+"F0.imprint","IMPRINT",EDGE,{"disambiguationData":[TD([[makeQuery(id+"F0.imprint","INTERSECT",VERTEX,{"disambiguationData":[OD(0.0)],"derivedFrom":[subQ0,sQuery(id+"F0.wireOp",EDGE,"E12")]}),1.0]])],"derivedFrom":subQ0})])],"isStart":true});}
            var Q12;
            {var subQ0=sQuery(id+"F0.wireOp",EDGE,"E6");Q12=makeQuery(id+"F1.opExtrude","CAP_EDGE",EDGE,{"disambiguationData":[OSD([subQ0]),TDD([makeQuery(id+"F0.imprint","IMPRINT",EDGE,{"disambiguationData":[TD([[makeQuery(id+"F0.imprint","INTERSECT",VERTEX,{"derivedFrom":[subQ0,sQuery(id+"F0.wireOp",EDGE,"E12")]}),-1.0]])],"derivedFrom":subQ0}),makeQuery(id+"F0.imprint","IMPRINT",EDGE,{"disambiguationData":[TD([[makeQuery(id+"F0.imprint","INTERSECT",VERTEX,{"derivedFrom":[subQ0,sQuery(id+"F0.wireOp",EDGE,"E20")]}),1.0]])],"derivedFrom":subQ0})])],"isStart":true});}
            var Q13;
            {var subQ0=sQuery(id+"F0.wireOp",EDGE,"E7");var subQ1=makeQuery(id+"F0.imprint","INTERSECT",VERTEX,{"disambiguationData":[OD(1.0)],"derivedFrom":[sQuery(id+"F0.wireOp",EDGE,"E2"),subQ0]});Q13=makeQuery(id+"F1.opExtrude","CAP_EDGE",EDGE,{"disambiguationData":[OSD([subQ0]),TDD([makeQuery(id+"F0.imprint","IMPRINT",EDGE,{"disambiguationData":[TD([[subQ1,1.0]])],"derivedFrom":subQ0}),makeQuery(id+"F0.imprint","IMPRINT",EDGE,{"disambiguationData":[TD([[makeQuery(id+"F0.imprint","INTERSECT",VERTEX,{"disambiguationData":[OD(0.0)],"derivedFrom":[subQ0,sQuery(id+"F0.wireOp",EDGE,"E11")]}),1.0]])],"derivedFrom":subQ0})])],"isStart":true});}
            var Q14;
            {var subQ0=sQuery(id+"F0.wireOp",EDGE,"E7");var subQ1=makeQuery(id+"F0.imprint","INTERSECT",VERTEX,{"disambiguationData":[OD(0.0)],"derivedFrom":[sQuery(id+"F0.wireOp",EDGE,"E2"),subQ0]});Q14=makeQuery(id+"F1.opExtrude","CAP_EDGE",EDGE,{"disambiguationData":[OSD([subQ0]),TDD([makeQuery(id+"F0.imprint","IMPRINT",EDGE,{"disambiguationData":[TD([[makeQuery(id+"F0.imprint","INTERSECT",VERTEX,{"disambiguationData":[OD(0.0)],"derivedFrom":[subQ0,sQuery(id+"F0.wireOp",EDGE,"E14")]}),-1.0]])],"derivedFrom":subQ0}),makeQuery(id+"F0.imprint","IMPRINT",EDGE,{"disambiguationData":[TD([[subQ1,-1.0]])],"derivedFrom":subQ0})])],"isStart":true});}
            var Q15;
            {var subQ0=sQuery(id+"F0.wireOp",EDGE,"E1");Q15=makeQuery(id+"F1.opExtrude","CAP_EDGE",EDGE,{"disambiguationData":[OSD([subQ0]),TDD([makeQuery(id+"F0.imprint","IMPRINT",EDGE,{"disambiguationData":[TD([[makeQuery(id+"F0.imprint","INTERSECT",VERTEX,{"derivedFrom":[subQ0,sQuery(id+"F0.wireOp",EDGE,"E9")]}),-1.0]])],"derivedFrom":subQ0})])],"isStart":true});}
            var Q16;
            {var subQ0=sQuery(id+"F0.wireOp",EDGE,"E8");Q16=makeQuery(id+"F1.opExtrude","CAP_EDGE",EDGE,{"disambiguationData":[OSD([subQ0]),TDD([makeQuery(id+"F0.imprint","IMPRINT",EDGE,{"disambiguationData":[TD([[makeQuery(id+"F0.imprint","INTERSECT",VERTEX,{"disambiguationData":[OD(0.0)],"derivedFrom":[subQ0,sQuery(id+"F0.wireOp",EDGE,"E9")]}),1.0]])],"derivedFrom":subQ0}),makeQuery(id+"F0.imprint","IMPRINT",EDGE,{"disambiguationData":[TD([[makeQuery(id+"F0.imprint","INTERSECT",VERTEX,{"disambiguationData":[OD(0.0)],"derivedFrom":[subQ0,sQuery(id+"F0.wireOp",EDGE,"E16")]}),-1.0]])],"derivedFrom":subQ0})])],"isStart":true});}
            var Q17;
            {var subQ0=sQuery(id+"F0.wireOp",EDGE,"E8");Q17=makeQuery(id+"F1.opExtrude","CAP_EDGE",EDGE,{"disambiguationData":[OSD([subQ0]),TDD([makeQuery(id+"F0.imprint","IMPRINT",EDGE,{"disambiguationData":[TD([[makeQuery(id+"F0.imprint","INTERSECT",VERTEX,{"disambiguationData":[OD(0.0)],"derivedFrom":[subQ0,sQuery(id+"F0.wireOp",EDGE,"E10")]}),-1.0]])],"derivedFrom":subQ0}),makeQuery(id+"F0.imprint","IMPRINT",EDGE,{"disambiguationData":[TD([[makeQuery(id+"F0.imprint","INTERSECT",VERTEX,{"derivedFrom":[subQ0,sQuery(id+"F0.wireOp",EDGE,"E15")]}),1.0]])],"derivedFrom":subQ0})])],"isStart":true});}
            var Q18;
            Q18=makeQuery(id+"F1.opExtrude","CAP_EDGE",EDGE,{"disambiguationData":[OSD([sQuery(id+"F0.wireOp",EDGE,"E15")])],"isStart":true});
            var Q19;
            {var subQ0=sQuery(id+"F0.wireOp",EDGE,"E16");var subQ1=sQuery(id+"F0.wireOp",EDGE,"E15");Q19=makeQuery(id+"F2.opFillet","BLEND_EDGE",EDGE,{"blendedFrom":[makeQuery(id+"F1.opExtrude","SWEPT_EDGE",EDGE,{"disambiguationData":[OSD([subQ1,subQ0,sQuery(id+"F0.wireOp",EDGE,"E18")])]}),makeQuery(id+"F1.opExtrude","CAP_FACE",FACE,{"disambiguationData":[OSD([sQuery(id+"F0.wireOp",EDGE,"E0"),sQuery(id+"F0.wireOp",EDGE,"E1"),sQuery(id+"F0.wireOp",EDGE,"E3"),sQuery(id+"F0.wireOp",EDGE,"E4"),sQuery(id+"F0.wireOp",EDGE,"E5"),sQuery(id+"F0.wireOp",EDGE,"E6"),sQuery(id+"F0.wireOp",EDGE,"E7"),sQuery(id+"F0.wireOp",EDGE,"E8"),sQuery(id+"F0.wireOp",EDGE,"E9"),sQuery(id+"F0.wireOp",EDGE,"E10"),sQuery(id+"F0.wireOp",EDGE,"E11"),sQuery(id+"F0.wireOp",EDGE,"E12"),sQuery(id+"F0.wireOp",EDGE,"E13"),sQuery(id+"F0.wireOp",EDGE,"E14"),subQ1,subQ0,sQuery(id+"F0.wireOp",EDGE,"E20"),sQuery(id+"F0.wireOp",EDGE,"E21"),sQuery(id+"F0.wireOp",EDGE,"E23"),sQuery(id+"F0.wireOp",EDGE,"E24")])],"isStart":true})],"blendedInto":[makeQuery(id+"F1.opExtrude","CAP_FACE",FACE,{"disambiguationData":[OSD([sQuery(id+"F0.wireOp",EDGE,"E0"),sQuery(id+"F0.wireOp",EDGE,"E1"),sQuery(id+"F0.wireOp",EDGE,"E3"),sQuery(id+"F0.wireOp",EDGE,"E4"),sQuery(id+"F0.wireOp",EDGE,"E5"),sQuery(id+"F0.wireOp",EDGE,"E6"),sQuery(id+"F0.wireOp",EDGE,"E7"),sQuery(id+"F0.wireOp",EDGE,"E8"),sQuery(id+"F0.wireOp",EDGE,"E9"),sQuery(id+"F0.wireOp",EDGE,"E10"),sQuery(id+"F0.wireOp",EDGE,"E11"),sQuery(id+"F0.wireOp",EDGE,"E12"),sQuery(id+"F0.wireOp",EDGE,"E13"),sQuery(id+"F0.wireOp",EDGE,"E14"),subQ1,subQ0,sQuery(id+"F0.wireOp",EDGE,"E20"),sQuery(id+"F0.wireOp",EDGE,"E21"),sQuery(id+"F0.wireOp",EDGE,"E23"),sQuery(id+"F0.wireOp",EDGE,"E24")])],"isStart":true})]});}
            var Q20;
            Q20=makeQuery(id+"F1.opExtrude","CAP_EDGE",EDGE,{"disambiguationData":[OSD([sQuery(id+"F0.wireOp",EDGE,"E16")])],"isStart":true});
            var Q21;
            Q21=makeQuery(id+"F1.opExtrude","CAP_EDGE",EDGE,{"disambiguationData":[OSD([sQuery(id+"F0.wireOp",EDGE,"E23")])],"isStart":true});
            var Q22;
            Q22=makeQuery(id+"F1.opExtrude","CAP_EDGE",EDGE,{"disambiguationData":[OSD([sQuery(id+"F0.wireOp",EDGE,"E24")])],"isStart":true});
            var Q23;
            {var subQ0=sQuery(id+"F0.wireOp",EDGE,"E24");var subQ1=sQuery(id+"F0.wireOp",EDGE,"E23");Q23=makeQuery(id+"F2.opFillet","BLEND_EDGE",EDGE,{"blendedFrom":[makeQuery(id+"F1.opExtrude","SWEPT_EDGE",EDGE,{"disambiguationData":[OSD([sQuery(id+"F0.wireOp",EDGE,"E17"),subQ1,subQ0])]}),makeQuery(id+"F1.opExtrude","CAP_FACE",FACE,{"disambiguationData":[OSD([sQuery(id+"F0.wireOp",EDGE,"E0"),sQuery(id+"F0.wireOp",EDGE,"E1"),sQuery(id+"F0.wireOp",EDGE,"E3"),sQuery(id+"F0.wireOp",EDGE,"E4"),sQuery(id+"F0.wireOp",EDGE,"E5"),sQuery(id+"F0.wireOp",EDGE,"E6"),sQuery(id+"F0.wireOp",EDGE,"E7"),sQuery(id+"F0.wireOp",EDGE,"E8"),sQuery(id+"F0.wireOp",EDGE,"E9"),sQuery(id+"F0.wireOp",EDGE,"E10"),sQuery(id+"F0.wireOp",EDGE,"E11"),sQuery(id+"F0.wireOp",EDGE,"E12"),sQuery(id+"F0.wireOp",EDGE,"E13"),sQuery(id+"F0.wireOp",EDGE,"E14"),sQuery(id+"F0.wireOp",EDGE,"E15"),sQuery(id+"F0.wireOp",EDGE,"E16"),sQuery(id+"F0.wireOp",EDGE,"E20"),sQuery(id+"F0.wireOp",EDGE,"E21"),subQ1,subQ0])],"isStart":true})],"blendedInto":[makeQuery(id+"F1.opExtrude","CAP_FACE",FACE,{"disambiguationData":[OSD([sQuery(id+"F0.wireOp",EDGE,"E0"),sQuery(id+"F0.wireOp",EDGE,"E1"),sQuery(id+"F0.wireOp",EDGE,"E3"),sQuery(id+"F0.wireOp",EDGE,"E4"),sQuery(id+"F0.wireOp",EDGE,"E5"),sQuery(id+"F0.wireOp",EDGE,"E6"),sQuery(id+"F0.wireOp",EDGE,"E7"),sQuery(id+"F0.wireOp",EDGE,"E8"),sQuery(id+"F0.wireOp",EDGE,"E9"),sQuery(id+"F0.wireOp",EDGE,"E10"),sQuery(id+"F0.wireOp",EDGE,"E11"),sQuery(id+"F0.wireOp",EDGE,"E12"),sQuery(id+"F0.wireOp",EDGE,"E13"),sQuery(id+"F0.wireOp",EDGE,"E14"),sQuery(id+"F0.wireOp",EDGE,"E15"),sQuery(id+"F0.wireOp",EDGE,"E16"),sQuery(id+"F0.wireOp",EDGE,"E20"),sQuery(id+"F0.wireOp",EDGE,"E21"),subQ1,subQ0])],"isStart":true})]});}
            fillet(context, id + "F4", {"entities" : qUnion([Q0, Q1, Q2, Q3, Q4, Q5, Q6, Q7, Q8, Q9, Q10, Q11, Q12, Q13, Q14, Q15, Q16, Q17, Q18, Q19, Q20, Q21, Q22, Q23]), "radius" : 3 * mm, "tangentPropagation" : true, "allowEdgeOverflow" : false});
        }
    });
